# Revit family: DoorOperators_Genie_GCL-GCX
name_source: partatom
category: Generic Models
units: mm (PartAtom-declared; Revit-internal decimal feet)

## family parameters
Always vertical = Yes
Can host rebar = No
Classification Number = 23.30.10.11
Cut with Voids When Loaded = No
Maintain Annotation Orientation = No
Part Type = Normal
Room Calculation Point = No
Round Connector Dimension = Use Diameter
Shared = No
Work Plane-Based = Yes

## types (1)
- 1/2 HP / 115V / 1 Phase
    Assembly Code = 23.30.10.11
    Construction Details = http://commercial.geniecompany.com
    Default Elevation = 48"
    Depth = 14 3/8"
    Description = Genie GCL-GCX Commercial Overhead Door Operator
    Hardware Material = Metal - Aluminum - GenieCommercial
    Height = 9 11/16"
    Installation-Fabrication = http://commercial.geniecompany.com
    Keynote = 08 71 13
    Length = 18 1/8"
    MEP Amperage = 7 A
    Manufacturer = Genie Company
    Manufacturer Fax = 800-221-0132
    Manufacturer Website = http://commercial.geniecompany.com
    Model = GCL-GCX
    Operator Material = Metal - Steel - GenieCommercial
    Product Data = http://www.arcat.com
    Revision = R0_11-2017
    Sales Information = http://www.geniecompany.com
    Specification = http://www.arcat.com
    Test Data = http://commercial.geniecompany.com
    URL = http://commercial.geniecompany.com
    Voltage_MEP = 11 V

## geometry (parser evidence)
native form markers: Sweep x3
no freeform markers — native parametric forms only
